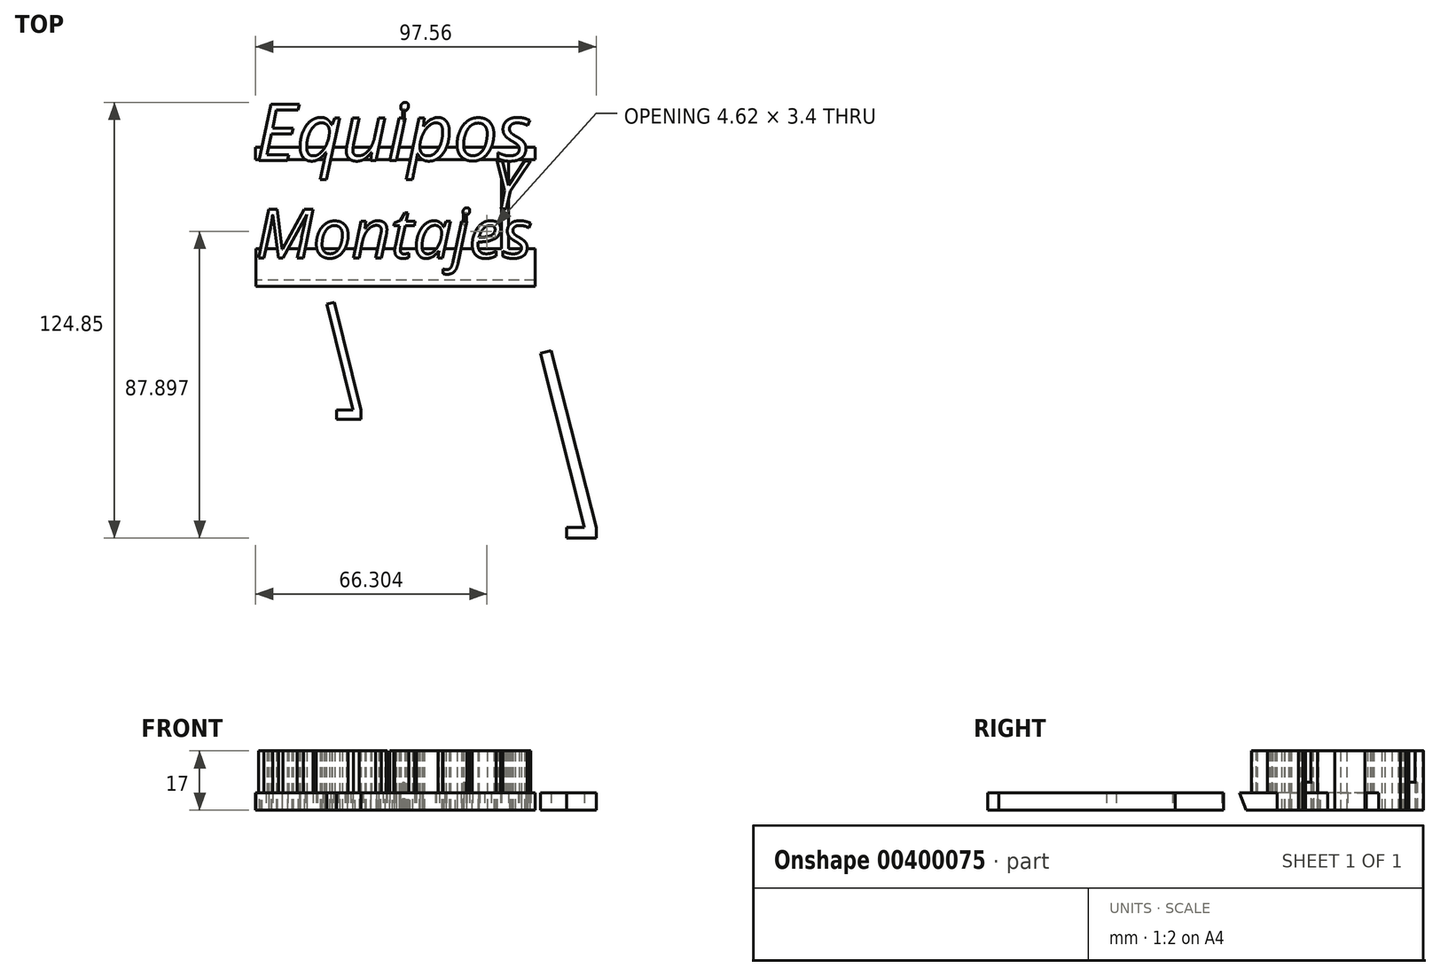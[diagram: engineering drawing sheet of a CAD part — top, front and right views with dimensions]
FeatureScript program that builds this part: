
annotation { "Feature Type Name" : "Feature", "Feature Type Description" : "" }
export const myFeature = defineFeature(function(context is Context, id is Id, definition is map)
    precondition{}
    {
        {
            var Q0;
            Q0=qCreatedBy(makeId("Top.planeOp"),FACE);
            var sketch = newSketch(context, id + "F0", { "sketchPlane" : qUnion([Q0])});
            skText(sketch, "E0", { "text": "Equipos", "fontName": "OpenSans-Italic.ttf"});
            skText(sketch, "E1", { "text": "Y", "fontName": "OpenSans-Italic.ttf"});
            skText(sketch, "E2", { "text": "Montajes", "fontName": "OpenSans-Italic.ttf"});
            const initialGuessF0  = {"E0": [-0.08, 0.04068, 1, 0, 0.01631], "E1": [-0.01268, 0.02685, 1, 0, 0.01383], "E2": [-0.08, 0.01275, 1, 0, 0.0141]};
            skSetInitialGuess(sketch, initialGuessF0);
            skSolve(sketch);
        }
        {
            var Q0;
            Q0=qCreatedBy(makeId("Top.planeOp"),FACE);
            var sketch = newSketch(context, id + "F1", { "sketchPlane" : qUnion([Q0])});
            skLineSegment(sketch, "E3.bottom", {"start": v(-80.07, 44.45) * mm, "end": v(0, 44.45) * mm});
            skLineSegment(sketch, "E3.top", {"start": v(-80.07, 40.86) * mm, "end": v(0, 40.86) * mm});
            skLineSegment(sketch, "E3.left", {"start": v(-80.07, 44.45) * mm, "end": v(-80.07, 40.86) * mm});
            skLineSegment(sketch, "E3.right", {"start": v(0, 44.45) * mm, "end": v(0, 40.86) * mm});
            skLineSegment(sketch, "E4.bottom", {"start": v(-7.55, 44.45) * mm, "end": v(-9.6, 44.45) * mm});
            skLineSegment(sketch, "E4.top", {"start": v(-7.55, 12.88) * mm, "end": v(-9.6, 12.88) * mm});
            skLineSegment(sketch, "E4.left", {"start": v(-7.55, 44.45) * mm, "end": v(-7.55, 12.88) * mm});
            skLineSegment(sketch, "E4.right", {"start": v(-9.6, 44.45) * mm, "end": v(-9.6, 12.88) * mm});
            skLineSegment(sketch, "E5.bottom", {"start": v(-79.97, 15.36) * mm, "end": v(0, 15.36) * mm});
            skLineSegment(sketch, "E5.top", {"start": v(-79.97, 4.61) * mm, "end": v(0, 4.61) * mm});
            skLineSegment(sketch, "E5.left", {"start": v(-79.97, 15.36) * mm, "end": v(-79.97, 4.61) * mm});
            skLineSegment(sketch, "E5.right", {"start": v(0, 15.36) * mm, "end": v(0, 4.61) * mm});
            skSolve(sketch);
        }
        {
            var Q0;
            Q0 = qSketchRegion(id + "F1", true);
            extrude(context, id + "F2", {"entities" : qUnion([Q0]), "depth" : 5 * mm});
        }
        {
            var Q0;
            Q0=makeQuery(id+"F2.opExtrude","CAP_EDGE",EDGE,{"disambiguationData":[OSD([sQuery(id+"F1.wireOp",EDGE,"E5.top")])],"isStart":true});
            chamfer(context, id + "F3", {"entities" : qUnion([Q0]), "chamferType" : ChamferType.OFFSET_ANGLE, "width" : 5 * mm, "oppositeDirection" : false, "angle" : 20 * degree, "tangentPropagation" : true});
        }
        {
            var Q0;
            Q0 = qSketchRegion(id + "F0", true);
            extrude(context, id + "F4", {"entities" : qUnion([Q0]), "operationType" : NewBodyOperationType.ADD, "depth" : 17 * mm});
        }
        {
            var Q0;
            Q0=qCreatedBy(makeId("Top.planeOp"),FACE);
            var sketch = newSketch(context, id + "F5", { "sketchPlane" : qUnion([Q0])});
            skLineSegment(sketch, "E6.bottom", {"start": v(-37.94, 55.51) * mm, "end": v(-37.39, 55.51) * mm});
            skLineSegment(sketch, "E6.top", {"start": v(-37.94, 52) * mm, "end": v(-37.39, 52) * mm});
            skLineSegment(sketch, "E6.left", {"start": v(-37.94, 55.51) * mm, "end": v(-37.94, 52) * mm});
            skLineSegment(sketch, "E6.right", {"start": v(-37.39, 55.51) * mm, "end": v(-37.39, 52) * mm});
            skLineSegment(sketch, "E7.bottom", {"start": v(-20.5, 25.74) * mm, "end": v(-19.68, 25.74) * mm});
            skLineSegment(sketch, "E7.top", {"start": v(-20.5, 22.22) * mm, "end": v(-19.68, 22.22) * mm});
            skLineSegment(sketch, "E7.left", {"start": v(-20.5, 25.74) * mm, "end": v(-20.5, 22.22) * mm});
            skLineSegment(sketch, "E7.right", {"start": v(-19.68, 25.74) * mm, "end": v(-19.68, 22.22) * mm});
            skSolve(sketch);
        }
        {
            var Q0;
            Q0 = qSketchRegion(id + "F5", true);
            extrude(context, id + "F6", {"entities" : qUnion([Q0]), "depth" : 8 * mm});
        }
        {
            var Q0;
            Q0=qCreatedBy(makeId("Top.planeOp"),FACE);
            var sketch = newSketch(context, id + "F7", { "sketchPlane" : qUnion([Q0])});
            skLineSegment(sketch, "E8.bottom", {"start": v(-56.92, -30.8) * mm, "end": v(-49.9, -30.8) * mm});
            skLineSegment(sketch, "E8.top", {"start": v(-56.92, -33.53) * mm, "end": v(-49.9, -33.53) * mm});
            skLineSegment(sketch, "E8.left", {"start": v(-56.92, -30.8) * mm, "end": v(-56.92, -33.53) * mm});
            skLineSegment(sketch, "E8.right", {"start": v(-49.9, -30.8) * mm, "end": v(-49.9, -33.53) * mm});
            skLineSegment(sketch, "E9", {"start": v(-49.9, -30.8) * mm, "end": v(-57.5, 0) * mm});
            skLineSegment(sketch, "E10", {"start": v(-57.5, 0) * mm, "end": v(-59.66, -0.53) * mm});
            skLineSegment(sketch, "E11", {"start": v(-59.66, -0.53) * mm, "end": v(-52.2, -30.8) * mm});
            skSolve(sketch);
        }
        {
            var Q0;
            Q0=makeQuery(id+"F7.imprint","IMPRINT",FACE,{"disambiguationData":[TD([[makeQuery(id+"F7.imprint","IMPRINT",EDGE,{"derivedFrom":sQuery(id+"F7.wireOp",EDGE,"E8.top")}),1.0]])]});
            var Q1;
            {var subQ0=sQuery(id+"F7.wireOp",EDGE,"E9");Q1=makeQuery(id+"F7.imprint","IMPRINT",FACE,{"disambiguationData":[TD([[makeQuery(id+"F7.imprint","IMPRINT",EDGE,{"derivedFrom":subQ0}),1.0]])]});}
            extrude(context, id + "F8", {"entities" : qUnion([Q0, Q1]), "depth" : 5 * mm});
        }
        {
            var Q0;
            Q0=qCreatedBy(makeId("Top.planeOp"),FACE);
            var sketch = newSketch(context, id + "F9", { "sketchPlane" : qUnion([Q0])});
            skLineSegment(sketch, "E12.bottom", {"start": v(8.98, -64.43) * mm, "end": v(17.5, -64.43) * mm});
            skLineSegment(sketch, "E12.top", {"start": v(8.98, -67.54) * mm, "end": v(17.5, -67.54) * mm});
            skLineSegment(sketch, "E12.left", {"start": v(8.98, -64.43) * mm, "end": v(8.98, -67.54) * mm});
            skLineSegment(sketch, "E12.right", {"start": v(17.5, -64.43) * mm, "end": v(17.5, -67.54) * mm});
            skLineSegment(sketch, "E13", {"start": v(17.5, -64.43) * mm, "end": v(4.63, -13.8) * mm});
            skLineSegment(sketch, "E14", {"start": v(4.63, -13.8) * mm, "end": v(1.5, -14.6) * mm});
            skLineSegment(sketch, "E15", {"start": v(1.5, -14.6) * mm, "end": v(14.17, -64.43) * mm});
            skSolve(sketch);
        }
        {
            var Q0;
            Q0=makeQuery(id+"F9.imprint","IMPRINT",FACE,{"disambiguationData":[TD([[makeQuery(id+"F9.imprint","IMPRINT",EDGE,{"derivedFrom":sQuery(id+"F9.wireOp",EDGE,"E12.top")}),1.0]])]});
            var Q1;
            {var subQ0=sQuery(id+"F9.wireOp",EDGE,"E13");Q1=makeQuery(id+"F9.imprint","IMPRINT",FACE,{"disambiguationData":[TD([[makeQuery(id+"F9.imprint","IMPRINT",EDGE,{"derivedFrom":subQ0}),1.0]])]});}
            extrude(context, id + "F10", {"entities" : qUnion([Q0, Q1]), "depth" : 5 * mm});
        }
    });
